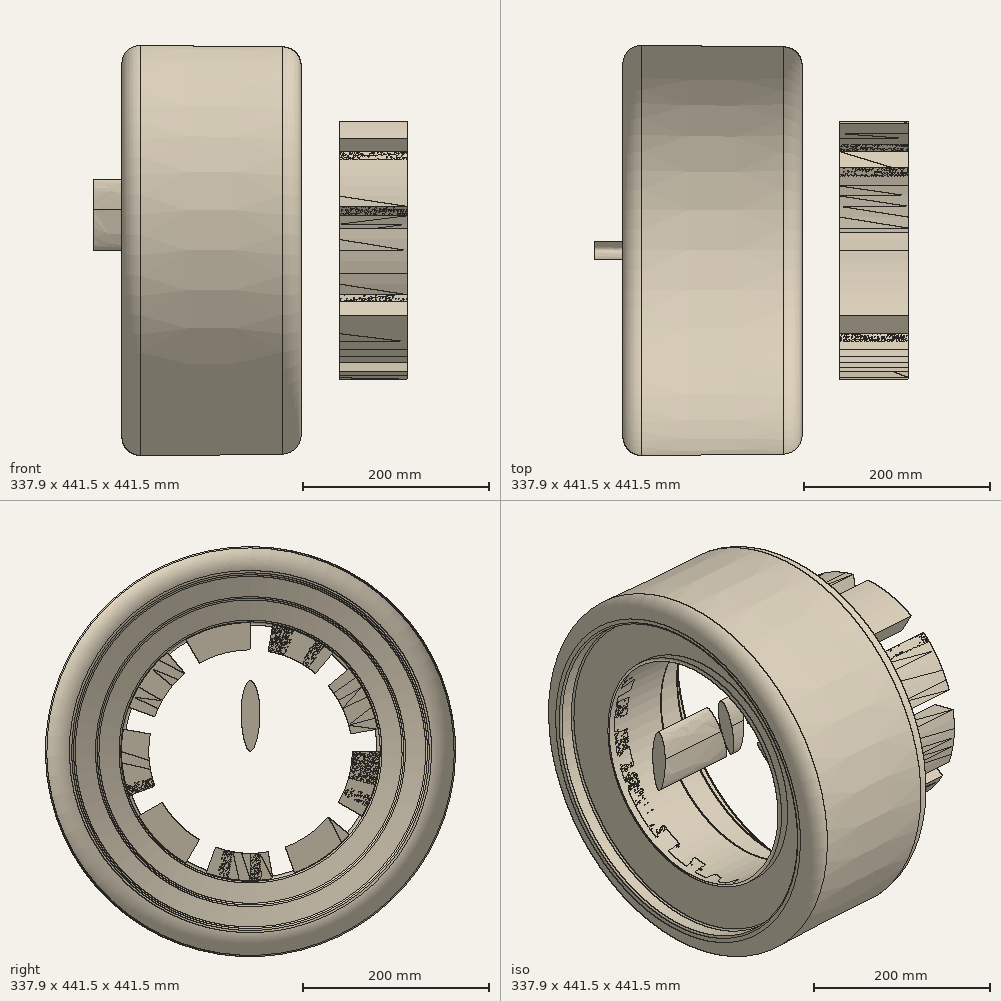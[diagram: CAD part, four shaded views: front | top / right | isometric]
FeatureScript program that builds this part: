
annotation { "Feature Type Name" : "Feature", "Feature Type Description" : "" }
export const myFeature = defineFeature(function(context is Context, id is Id, definition is map)
    precondition{}
    {
        {
            var Q0;
            Q0=qCreatedBy(makeId("Front.planeOp"),FACE);
            var sketch = newSketch(context, id + "F0", { "sketchPlane" : qUnion([Q0])});
            skLineSegment(sketch, "E0", {"start": v(-96.27, -197.5) * mm, "end": v(-95.57, -192.67) * mm});
            skLineSegment(sketch, "E1", {"start": v(-93.05, -190.5) * mm, "end": v(-78.02, -190.5) * mm});
            skLineSegment(sketch, "E2", {"start": v(-75.62, -188.77) * mm, "end": v(-59.05, -139.7) * mm});
            skLineSegment(sketch, "E3", {"start": v(-59.05, -139.7) * mm, "end": v(15.2, -139.7) * mm});
            skLineSegment(sketch, "E4", {"start": v(17.66, -141.57) * mm, "end": v(23.62, -163.23) * mm});
            skLineSegment(sketch, "E5", {"start": v(26.07, -165.1) * mm, "end": v(66.7, -165.1) * mm});
            skLineSegment(sketch, "E6", {"start": v(69.12, -166.91) * mm, "end": v(75.66, -188.69) * mm});
            skLineSegment(sketch, "E7", {"start": v(78.09, -190.5) * mm, "end": v(93.17, -190.5) * mm});
            skLineSegment(sketch, "E8", {"start": v(95.66, -192.54) * mm, "end": v(96.15, -195) * mm});
            skLineSegment(sketch, "E9", {"start": v(-59.05, -139.7) * mm, "end": v(-59.05, 0) * mm});
            skPoint(sketch, "E10.visualSharp", {"position": v(-95.25, -190.5) * mm});
            skArc(sketch, "E10.filletArc", {"start": v(-93.05, -190.5) * mm, "mid": v(-94.71, -191.12) * mm, "end": v(-95.57, -192.67) * mm});
            skPoint(sketch, "E11.visualSharp", {"position": v(-76.2, -190.5) * mm});
            skArc(sketch, "E11.filletArc", {"start": v(-78.02, -190.5) * mm, "mid": v(-76.54, -190.02) * mm, "end": v(-75.62, -188.77) * mm});
            skPoint(sketch, "E12.visualSharp", {"position": v(17.15, -139.7) * mm});
            skArc(sketch, "E12.filletArc", {"start": v(17.66, -141.57) * mm, "mid": v(16.75, -140.22) * mm, "end": v(15.2, -139.7) * mm});
            skPoint(sketch, "E13.visualSharp", {"position": v(24.13, -165.1) * mm});
            skArc(sketch, "E13.filletArc", {"start": v(23.62, -163.23) * mm, "mid": v(24.53, -164.58) * mm, "end": v(26.07, -165.1) * mm});
            skPoint(sketch, "E14.visualSharp", {"position": v(68.58, -165.1) * mm});
            skArc(sketch, "E14.filletArc", {"start": v(69.12, -166.91) * mm, "mid": v(68.2, -165.6) * mm, "end": v(66.7, -165.1) * mm});
            skPoint(sketch, "E15.visualSharp", {"position": v(76.2, -190.5) * mm});
            skArc(sketch, "E15.filletArc", {"start": v(75.66, -188.69) * mm, "mid": v(76.57, -190) * mm, "end": v(78.09, -190.5) * mm});
            skPoint(sketch, "E16.visualSharp", {"position": v(95.25, -190.5) * mm});
            skArc(sketch, "E16.filletArc", {"start": v(95.66, -192.54) * mm, "mid": v(94.78, -191.08) * mm, "end": v(93.17, -190.5) * mm});
            skLineSegment(sketch, "E17.MirrorCS", {"start": v(-59.05, 139.7) * mm, "end": v(-59.05, 0) * mm});
            skLineSegment(sketch, "E18.MirrorCS", {"start": v(-59.05, 139.7) * mm, "end": v(15.2, 139.7) * mm});
            skLineSegment(sketch, "E19.MirrorCS", {"start": v(17.66, 141.57) * mm, "end": v(23.62, 163.23) * mm});
            skLineSegment(sketch, "E20.MirrorCS", {"start": v(26.07, 165.1) * mm, "end": v(66.7, 165.1) * mm});
            skLineSegment(sketch, "E21.MirrorCS", {"start": v(69.12, 166.91) * mm, "end": v(75.66, 188.69) * mm});
            skLineSegment(sketch, "E22.MirrorCS", {"start": v(78.09, 190.5) * mm, "end": v(93.17, 190.5) * mm});
            skLineSegment(sketch, "E23.MirrorCS", {"start": v(95.66, 192.54) * mm, "end": v(96.15, 195) * mm});
            skLineSegment(sketch, "E24.MirrorCS", {"start": v(-75.62, 188.77) * mm, "end": v(-59.05, 139.7) * mm});
            skLineSegment(sketch, "E25.MirrorCS", {"start": v(-96.27, 197.5) * mm, "end": v(-95.57, 192.67) * mm});
            skArc(sketch, "E26.MirrorCS", {"start": v(-93.05, 190.5) * mm, "mid": v(-94.71, 191.12) * mm, "end": v(-95.57, 192.67) * mm});
            skArc(sketch, "E27.MirrorCS", {"start": v(-78.02, 190.5) * mm, "mid": v(-76.54, 190.02) * mm, "end": v(-75.62, 188.77) * mm});
            skArc(sketch, "E28.MirrorCS", {"start": v(17.66, 141.57) * mm, "mid": v(16.75, 140.22) * mm, "end": v(15.2, 139.7) * mm});
            skArc(sketch, "E29.MirrorCS", {"start": v(23.62, 163.23) * mm, "mid": v(24.53, 164.58) * mm, "end": v(26.07, 165.1) * mm});
            skArc(sketch, "E30.MirrorCS", {"start": v(69.12, 166.91) * mm, "mid": v(68.2, 165.6) * mm, "end": v(66.7, 165.1) * mm});
            skArc(sketch, "E31.MirrorCS", {"start": v(75.66, 188.69) * mm, "mid": v(76.57, 190) * mm, "end": v(78.09, 190.5) * mm});
            skArc(sketch, "E32.MirrorCS", {"start": v(95.66, 192.54) * mm, "mid": v(94.78, 191.08) * mm, "end": v(93.17, 190.5) * mm});
            skLineSegment(sketch, "E33.MirrorCS", {"start": v(-93.05, 190.5) * mm, "end": v(-78.02, 190.5) * mm});
            skFitSpline(sketch, "E34", {"points": [v(-99.7, 220.98) * mm, v(100.96, 219.07) * mm], "startDerivative": vector(200.66, -1.9) * mm, "endDerivative": vector(200.66, -1.9) * mm});
            skFitSpline(sketch, "E35", {"points": [v(-99.7, -220.98) * mm, v(100.96, -219.07) * mm], "startDerivative": vector(200.66, 1.9) * mm, "endDerivative": vector(200.66, 1.9) * mm});
            skArc(sketch, "E36.filletArc", {"start": v(-75.97, 220.75) * mm, "mid": v(-91.47, 213.8) * mm, "end": v(-96.27, 197.5) * mm});
            skArc(sketch, "E37.filletArc", {"start": v(96.15, 195) * mm, "mid": v(92, 211.8) * mm, "end": v(76.42, 219.3) * mm});
            skArc(sketch, "E38.filletArc", {"start": v(76.42, -219.3) * mm, "mid": v(92, -211.8) * mm, "end": v(96.15, -195) * mm});
            skArc(sketch, "E39.filletArc", {"start": v(-96.27, -197.5) * mm, "mid": v(-91.47, -213.8) * mm, "end": v(-75.97, -220.75) * mm});
            skLineSegment(sketch, "E40", {"start": v(-7.62, 139.7) * mm, "end": v(-7.62, -139.7) * mm});
            skLineSegment(sketch, "E41", {"start": v(-59.05, 0) * mm, "end": v(-7.62, 0) * mm});
            skSolve(sketch);
        }
        {
            var Q0;
            Q0=makeQuery(id+"F0.imprint","IMPRINT",FACE,{"disambiguationData":[TD([[makeQuery(id+"F0.imprint","IMPRINT",EDGE,{"derivedFrom":sQuery(id+"F0.wireOp",EDGE,"E0")}),-1.0]])]});
            var Q1;
            Q1=sQuery(id+"F0.wireOp",EDGE,"E41");
            revolve(context, id + "F1", {"surfaceOperationType" : NewSurfaceOperationType.NEW, "entities" : qUnion([Q0]), "axis" : qUnion([Q1]), "revolveType" : RevolveType.FULL});
        }
        {
            var Q0;
            Q0=qCreatedBy(makeId("Front.planeOp"),FACE);
            var sketch = newSketch(context, id + "F2", { "sketchPlane" : qUnion([Q0])});
            skLineSegment(sketch, "E42", {"start": v(-10.29, 0) * mm, "end": v(-39.19, 139.7) * mm});
            skLineSegment(sketch, "E43", {"start": v(-39.19, 139.7) * mm, "end": v(-68.78, 139.7) * mm});
            skLineSegment(sketch, "E44", {"start": v(-71.15, 136.25) * mm, "end": v(-19.1, 0) * mm});
            skLineSegment(sketch, "E45", {"start": v(-19.1, 0) * mm, "end": v(-10.29, 0) * mm});
            skPoint(sketch, "E46.visualSharp", {"position": v(-72.47, 139.7) * mm});
            skArc(sketch, "E46.filletArc", {"start": v(-68.78, 139.7) * mm, "mid": v(-70.87, 138.6) * mm, "end": v(-71.15, 136.25) * mm});
            skSolve(sketch);
        }
        {
            var Q0;
            Q0 = qSketchRegion(id + "F2", true);
            var Q1;
            Q1=sQuery(id+"F2.wireOp",EDGE,"E45");
            revolve(context, id + "F3", {"surfaceOperationType" : NewSurfaceOperationType.NEW, "entities" : qUnion([Q0]), "axis" : qUnion([Q1]), "revolveType" : RevolveType.FULL});
        }
        {
            var Q0;
            Q0=qCreatedBy(makeId("Front.planeOp"),FACE);
            var sketch = newSketch(context, id + "F4", { "sketchPlane" : qUnion([Q0])});
            skLineSegment(sketch, "E47.bottom", {"start": v(210.94, 138.9) * mm, "end": v(137.24, 138.9) * mm});
            skLineSegment(sketch, "E47.top", {"start": v(210.94, 109.53) * mm, "end": v(137.24, 109.53) * mm});
            skLineSegment(sketch, "E47.left", {"start": v(210.94, 138.9) * mm, "end": v(210.94, 109.53) * mm});
            skLineSegment(sketch, "E47.right", {"start": v(137.24, 138.9) * mm, "end": v(137.24, 109.53) * mm});
            skLineSegment(sketch, "E48", {"start": v(0, 0) * mm, "end": v(237.1, 0) * mm});
            skSolve(sketch);
        }
        {
            var Q0;
            Q0=makeQuery(id+"F4.imprint","IMPRINT",FACE,{"disambiguationData":[TD([[makeQuery(id+"F4.imprint","IMPRINT",EDGE,{"derivedFrom":sQuery(id+"F4.wireOp",EDGE,"E47.bottom")}),1.0]])]});
            var Q1;
            Q1=sQuery(id+"F4.wireOp",EDGE,"E48");
            revolve(context, id + "F5", {"surfaceOperationType" : NewSurfaceOperationType.NEW, "entities" : qUnion([Q0]), "axis" : qUnion([Q1]), "revolveType" : RevolveType.ONE_DIRECTION, "angle" : 30 * degree});
        }
        {
            var Q0;
            Q0=makeQuery(id+"F5.opRevolve","SWEPT_BODY",BODY,{"disambiguationData":[OSD([sQuery(id+"F4.wireOp",EDGE,"E47.bottom"),sQuery(id+"F4.wireOp",EDGE,"E47.top"),sQuery(id+"F4.wireOp",EDGE,"E47.left"),sQuery(id+"F4.wireOp",EDGE,"E47.right")])]});
            var Q1;
            Q1=makeQuery(id+"F3.opRevolve","SWEPT_FACE",FACE,{"disambiguationData":[OSD([sQuery(id+"F2.wireOp",EDGE,"E42")])]});
            circularPattern(context, id + "F6", {"entities" : qUnion([Q0]), "axis" : qUnion([Q1]), "angle" : 360 * degree, "instanceCount" : 9, "equalSpace" : true, "isCentered" : true});
        }
        {
            var Q0;
            Q0=qCreatedBy(makeId("Right.planeOp"),FACE);
            var sketch = newSketch(context, id + "F7", { "sketchPlane" : qUnion([Q0])});
            skPoint(sketch, "E49", {"position": v(0, 12.7) * mm});
            skPoint(sketch, "E50", {"position": v(0, 76.2) * mm});
            skPoint(sketch, "E51", {"position": v(-10.16, 44.45) * mm});
            skPoint(sketch, "E52", {"position": v(10.16, 44.45) * mm});
            skLineSegment(sketch, "E53", {"start": v(-59.76, 0) * mm, "end": v(59.49, 0) * mm});
            skLineSegment(sketch, "E54", {"start": v(-35.96, 44.45) * mm, "end": v(46.9, 44.45) * mm});
            skFitSpline(sketch, "E55", {"points": [v(0, 76.2) * mm, v(-10.16, 44.45) * mm, v(0, 0) * mm, v(10.16, 44.45) * mm, v(0, 76.2) * mm]});
            skSolve(sketch);
        }
        {
            var Q0;
            Q0 = qSketchRegion(id + "F7", true);
            extrude(context, id + "F8", {"entities" : qUnion([Q0]), "operationType" : NewBodyOperationType.ADD, "oppositeDirection" : true, "depth" : 127 * mm, "offsetDistance" : 25.4 * mm});
        }
    });
